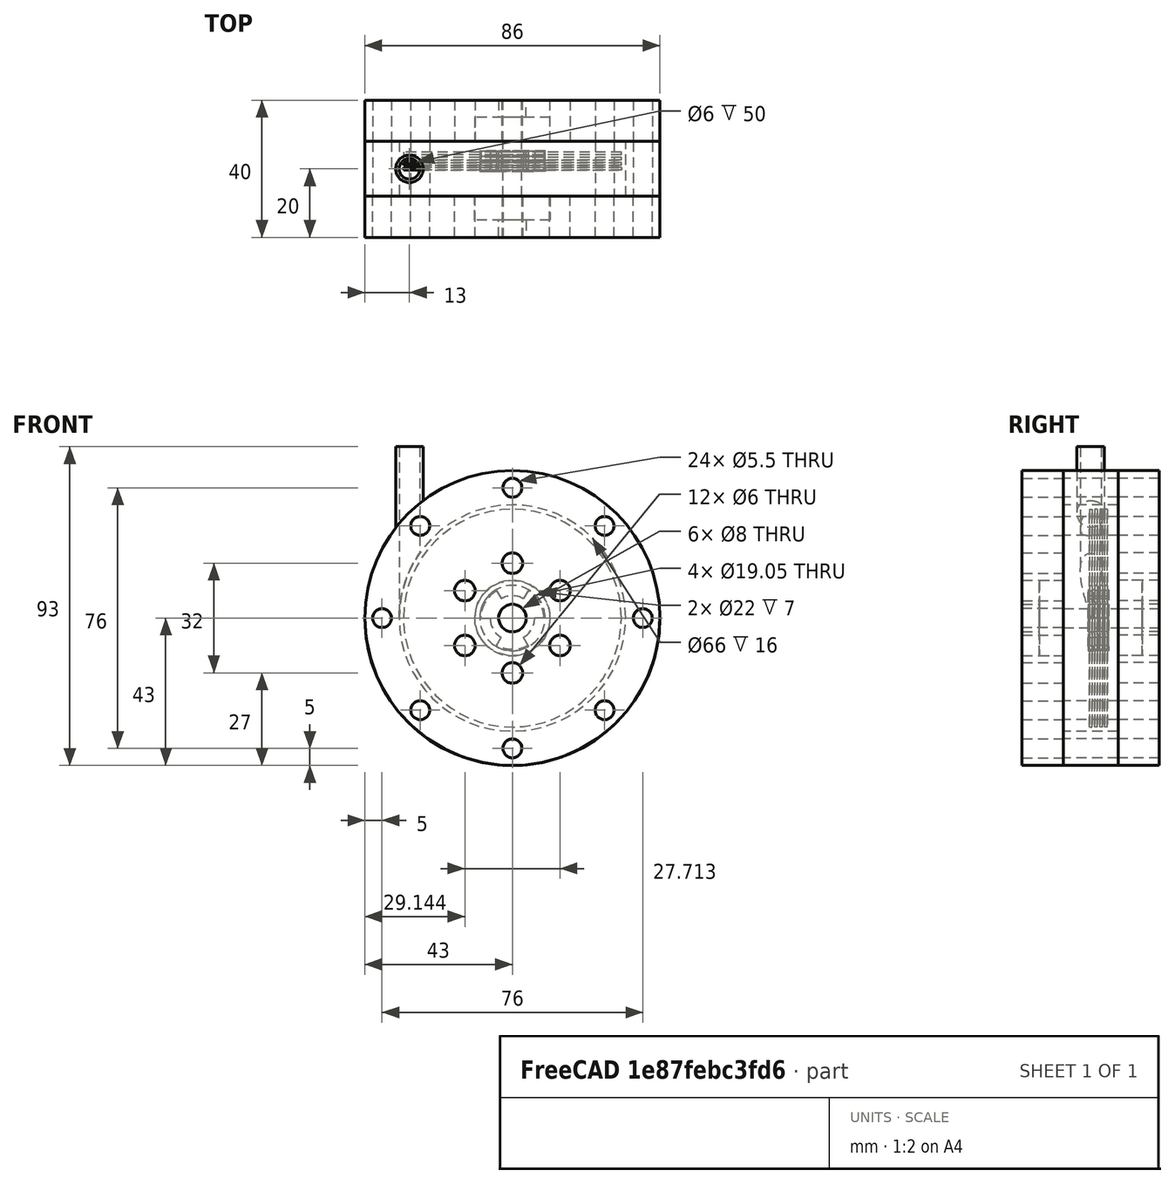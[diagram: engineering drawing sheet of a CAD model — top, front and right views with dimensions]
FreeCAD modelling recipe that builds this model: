
FCSTD DOCUMENT  (FreeCAD 0.17R13541 (Git))
Label: 特斯拉叶轮机 FEM
License: All rights reserved
LicenseURL: http://en.wikipedia.org/wiki/All_rights_reserved
objects: Sketcher::SketchObject×14, PartDesign::ShapeBinder×7, Part::Mirroring×7, Part::Feature×7, PartDesign::Pocket×6, PartDesign::Body×5, PartDesign::Pad×4, PartDesign::PolarPattern×4, PartDesign::Groove×2, Fem::FemMeshShapeNetgenObject×2, PartDesign::Revolution×1, Part::Compound×1, Fem::FemSolverObjectPython×1, Part::MultiFuse×1, Fem::FemAnalysis×1
note: 72 computed .brp shape members not serialized (recipe doc carries the construction recipe); baked Part::Feature solids carry a one-line shape summary decoded from their .brp

FEATURE [Sketcher::SketchObject] Sketch
  MapMode = 5
  Placement = pos=(0,0,0) rot=(1,0,0;1.5708rad)
  Support = -> [XZ_Plane]
  sketch-geometry (14):
    g0: Circle CenterX=0 CenterY=0 CenterZ=0 NormalX=0 NormalY=0 NormalZ=1 AngleXU=0 Radius=4
    g1: Circle CenterX=0 CenterY=0 CenterZ=0 NormalX=0 NormalY=0 NormalZ=1 AngleXU=0 Radius=9.525
    g2: Circle CenterX=0 CenterY=0 CenterZ=0 NormalX=0 NormalY=0 NormalZ=1 AngleXU=0 Radius=43
    g3: Circle CenterX=0 CenterY=0 CenterZ=0 NormalX=0 NormalY=0 NormalZ=1 AngleXU=0 Radius=31.75
    g4: Circle CenterX=0 CenterY=0 CenterZ=0 NormalX=0 NormalY=0 NormalZ=1 AngleXU=0 Radius=33
    g5: LineSegment [constr] StartX=-31.75 StartY=0 StartZ=0 EndX=-33 EndY=0 EndZ=0
    g6: LineSegment [constr] StartX=-33 StartY=0 StartZ=0 EndX=-43 EndY=0 EndZ=0
    g7: LineSegment StartX=-33 StartY=0 StartZ=0 EndX=-30 EndY=0 EndZ=0
    g8: LineSegment StartX=-30 StartY=0 StartZ=0 EndX=-30 EndY=50 EndZ=0
    g9: LineSegment StartX=-30 StartY=50 StartZ=0 EndX=-33 EndY=50 EndZ=0
    g10: LineSegment StartX=-33 StartY=50 StartZ=0 EndX=-33 EndY=0 EndZ=0
    g11: LineSegment StartX=-30 StartY=50 StartZ=0 EndX=-26 EndY=50 EndZ=0
    g12: LineSegment StartX=-26 StartY=50 StartZ=0 EndX=-26 EndY=0 EndZ=0
    g13: LineSegment StartX=-26 StartY=0 StartZ=0 EndX=-30 EndY=0 EndZ=0
  constraints (36):
    c: Coincident(g0,g-1)
    c: Coincident(g1,g-1)
    c: Coincident(g2,g-1)
    c: Coincident(g3,g-1)
    c: Radius(g0) = 4  '轴半径'
    c: Coincident(g4,g-1)
    c: Radius(g1) = 9.525
    c: Radius(g3) = 31.75  '盘片半径'
    c: PointOnObject(g5,g3)
    c: PointOnObject(g5,g4)
    c: Coincident(g6,g5)
    c: PointOnObject(g6,g2)
    c: Horizontal(g6)
    c: PointOnObject(g5,g-1)
    c: Horizontal(g5)
    c: DistanceX(g5,g5) = 1.25  '盘片与腔体内壁间隙'
    c: DistanceX(g6,g5) = 10  '腔体壁厚'
    c: Coincident(g7,g8)
    c: Coincident(g8,g9)
    c: Coincident(g9,g10)
    c: Coincident(g10,g7)
    c: Horizontal(g7)
    c: Horizontal(g9)
    c: Vertical(g8)
    c: Vertical(g10)
    c: Coincident(g7,g5)
    c: Horizontal(g11)
    c: Coincident(g11,g12)
    c: Vertical(g12)
    c: Coincident(g12,g13)
    c: Coincident(g13,g7)
    c: Horizontal(g13)
    c: Coincident(g11,g8)
    c: DistanceX(g8,g11) = 4  '进气管外圆半径'
    c: DistanceX(g9,g8) = 3  '进气管内孔半径'
    c: DistanceY(g5,g9) = 50
FEATURE [PartDesign::Body] Body  label="核心"
  Group = -> [Sketch]
  Origin = -> Origin
FEATURE [PartDesign::ShapeBinder] ShapeBinder
  Support = -> [Sketch]
FEATURE [Sketcher::SketchObject] Sketch001
  ExternalGeometry = -> [ShapeBinder]
  MapMode = 5
  Placement = pos=(0,0,0) rot=(1,0,0;1.5708rad)
  Support = -> [XZ_Plane001]
  sketch-geometry (1):
    g0: Circle CenterX=0 CenterY=0 CenterZ=0 NormalX=0 NormalY=0 NormalZ=1 AngleXU=0 Radius=43
  constraints (2):
    c: Coincident(g0,g-1)
    c: PointOnObject(g-3,g0)
FEATURE [PartDesign::Pad] Pad  label="叶片腔体"
  Length = 16
  Length2 = 100
  Midplane = true
  Placement = pos=(0,0,0) rot=(1,0,0;1.5708rad)
  Profile = -> Sketch001
  Type = 0
FEATURE [Sketcher::SketchObject] Sketch002
  ExternalGeometry = -> [ShapeBinder]
  MapMode = 5
  Placement = pos=(0,0,0) rot=(1,0,0;1.5708rad)
  Support = -> [XZ_Plane001]
  sketch-geometry (4):
    g0: LineSegment StartX=-26 StartY=0 StartZ=0 EndX=-30 EndY=0 EndZ=0
    g1: LineSegment StartX=-30 StartY=0 StartZ=0 EndX=-30 EndY=50 EndZ=0
    g2: LineSegment StartX=-30 StartY=50 StartZ=0 EndX=-26 EndY=50 EndZ=0
    g3: LineSegment StartX=-26 StartY=50 StartZ=0 EndX=-26 EndY=0 EndZ=0
  constraints (10):
    c: Coincident(g0,g1)
    c: Coincident(g1,g2)
    c: Coincident(g2,g3)
    c: Coincident(g3,g0)
    c: Horizontal(g0)
    c: Horizontal(g2)
    c: Vertical(g1)
    c: Vertical(g3)
    c: Coincident(g0,g-4)
    c: Coincident(g1,g-3)
FEATURE [PartDesign::Revolution] Revolution  label="进气管"
  Angle = 360
  Axis = (0,0,1)
  Base = (-30,0,0)
  BaseFeature = -> Pad
  Placement = pos=(0,0,0) rot=(1,0,0;1.5708rad)
  Profile = -> Sketch002
  ReferenceAxis = -> ShapeBinder [Edge14]
FEATURE [Sketcher::SketchObject] Sketch003
  ExternalGeometry = -> [ShapeBinder]
  MapMode = 5
  Placement = pos=(0,0,0) rot=(1,0,0;1.5708rad)
  Support = -> [XZ_Plane001]
  sketch-geometry (1):
    g0: Circle CenterX=0 CenterY=0 CenterZ=0 NormalX=0 NormalY=0 NormalZ=1 AngleXU=0 Radius=33
  constraints (2):
    c: Coincident(g0,g-1)
    c: PointOnObject(g-3,g0)
FEATURE [PartDesign::Pocket] Pocket  label="叶片腔孔"
  BaseFeature = -> Revolution
  Length = 5
  Length2 = 100
  Midplane = true
  Placement = pos=(0,0,0) rot=(1,0,0;1.5708rad)
  Profile = -> Sketch003
  Type = 1
FEATURE [Sketcher::SketchObject] Sketch004
  ExternalGeometry = -> [ShapeBinder]
  MapMode = 5
  Placement = pos=(0,0,0) rot=(1,0,0;1.5708rad)
  Support = -> [XZ_Plane001]
  sketch-geometry (4):
    g0: LineSegment StartX=-30 StartY=50 StartZ=0 EndX=-33 EndY=50 EndZ=0
    g1: LineSegment StartX=-33 StartY=50 StartZ=0 EndX=-33 EndY=0 EndZ=0
    g2: LineSegment StartX=-33 StartY=0 StartZ=0 EndX=-30 EndY=0 EndZ=0
    g3: LineSegment StartX=-30 StartY=0 StartZ=0 EndX=-30 EndY=50 EndZ=0
  constraints (10):
    c: Coincident(g0,g1)
    c: Coincident(g1,g2)
    c: Coincident(g2,g3)
    c: Coincident(g3,g0)
    c: Horizontal(g0)
    c: Horizontal(g2)
    c: Vertical(g1)
    c: Vertical(g3)
    c: Coincident(g0,g-3)
    c: Coincident(g1,g-4)
FEATURE [PartDesign::Groove] Groove  label="进气管孔"
  Angle = 360
  Axis = (0,0,1)
  Base = (-30,0,0)
  BaseFeature = -> Pocket
  Placement = pos=(0,0,0) rot=(1,0,0;1.5708rad)
  Profile = -> Sketch004
  ReferenceAxis = -> ShapeBinder [Edge13]
FEATURE [PartDesign::ShapeBinder] ShapeBinder001
  Support = -> [Sketch]
FEATURE [Sketcher::SketchObject] Sketch005
  ExternalGeometry = -> [ShapeBinder001]
  MapMode = 5
  Placement = pos=(0,0,0) rot=(1,0,0;1.5708rad)
  Support = -> [XZ_Plane002]
  sketch-geometry (2):
    g0: Circle CenterX=0 CenterY=0 CenterZ=0 NormalX=0 NormalY=0 NormalZ=1 AngleXU=0 Radius=9.525
    g1: Circle CenterX=0 CenterY=0 CenterZ=0 NormalX=0 NormalY=0 NormalZ=1 AngleXU=0 Radius=4
  constraints (4):
    c: Coincident(g0,g-1)
    c: Coincident(g1,g-1)
    c: Equal(g1,g-4)
    c: Equal(g-3,g0)
FEATURE [PartDesign::Pad] Pad001  label="分流片基体"
  Length = 1.5
  Length2 = 100
  Midplane = true
  Placement = pos=(0,0,0) rot=(1,0,0;1.5708rad)
  Profile = -> Sketch005
  Type = 0
FEATURE [Sketcher::SketchObject] Sketch006
  ExternalGeometry = -> [ShapeBinder001]
  MapMode = 5
  Placement = pos=(0,0,0) rot=(1,0,0;1.5708rad)
  Support = -> [XZ_Plane002]
  sketch-geometry (8):
    g0: LineSegment [constr] StartX=0 StartY=0 StartZ=0 EndX=4.7625 EndY=8.24889 EndZ=0
    g1: LineSegment [constr] StartX=4.7625 StartY=8.24889 StartZ=0 EndX=-4.7625 EndY=8.24889 EndZ=0
    g2: LineSegment [constr] StartX=-4.7625 StartY=8.24889 StartZ=0 EndX=0 EndY=0 EndZ=0
    g3: Circle [constr] CenterX=0 CenterY=5.49926 CenterZ=0 NormalX=0 NormalY=0 NormalZ=1 AngleXU=0 Radius=5.49926
    g4: ArcOfCircle CenterX=0 CenterY=0 CenterZ=0 NormalX=0 NormalY=0 NormalZ=1 AngleXU=0 Radius=6.5 StartAngle=1.0472 EndAngle=2.0944
    g5: ArcOfCircle CenterX=0 CenterY=0 CenterZ=0 NormalX=0 NormalY=0 NormalZ=1 AngleXU=0 Radius=9.525 StartAngle=1.0472 EndAngle=2.0944
    g6: LineSegment StartX=-4.7625 StartY=8.24889 StartZ=0 EndX=-3.25 EndY=5.62917 EndZ=0
    g7: LineSegment StartX=4.7625 StartY=8.24889 StartZ=0 EndX=3.25 EndY=5.62917 EndZ=0
  constraints (23):
    c: Coincident(g0,g1)
    c: Coincident(g1,g2)
    c: Coincident(g2,g0)
    c: Equal(g0,g1)
    c: Equal(g0,g2)
    c: PointOnObject(g0,g3)
    c: PointOnObject(g1,g3)
    c: PointOnObject(g2,g3)
    c: PointOnObject(g3,g-2)
    c: Coincident(g2,g-1)
    c: PointOnObject(g0,g-3)
    c: Coincident(g4,g-1)
    c: Radius(g4) = 6.5
    c: Coincident(g5,g-1)
    c: Equal(g5,g-3)
    c: PointOnObject(g5,g0)
    c: PointOnObject(g5,g1)
    c: PointOnObject(g4,g0)
    c: PointOnObject(g4,g2)
    c: Coincident(g6,g1)
    c: Coincident(g6,g4)
    c: Coincident(g7,g0)
    c: Coincident(g7,g4)
FEATURE [PartDesign::Pocket] Pocket001  label="分流槽"
  BaseFeature = -> Pad001
  Length = 5
  Length2 = 100
  Midplane = true
  Placement = pos=(0,0,0) rot=(1,0,0;1.5708rad)
  Profile = -> Sketch006
  Type = 1
FEATURE [PartDesign::PolarPattern] PolarPattern  label="分流槽环形阵列"
  Angle = 360
  Axis = -> Sketch006 [N_Axis]
  BaseFeature = -> Pocket001
  Occurrences = 3
  Originals = -> [Pocket001]
  Placement = pos=(0,0,0) rot=(1,0,0;1.5708rad)
FEATURE [Sketcher::SketchObject] Sketch007
  MapMode = 5
  Placement = pos=(0,0,0) rot=(0.57735,0.57735,0.57735;2.0944rad)
  Support = -> [YZ_Plane002]
  sketch-geometry (1):
    g0: Circle CenterX=0 CenterY=9.7 CenterZ=0 NormalX=0 NormalY=0 NormalZ=1 AngleXU=0 Radius=0.5
  constraints (3):
    c: PointOnObject(g0,g-2)
    c: Radius(g0) = 0.5
    c: DistanceY(g-1,g0) = 9.7
FEATURE [PartDesign::Groove] Groove001  label="扶持槽"
  Angle = 360
  Axis = (0,1,0)
  Base = (0,0,0)
  BaseFeature = -> PolarPattern
  Placement = pos=(0,0,0) rot=(1,0,0;1.5708rad)
  Profile = -> Sketch007
  ReferenceAxis = -> Y_Axis002
FEATURE [PartDesign::Body] Body002  label="分流片"
  Group = -> [ShapeBinder001,Sketch005,Pad001,Sketch006,Pocket001,PolarPattern,Sketch007,Groove001]
  Origin = -> Origin002
  Tip = -> Groove001
FEATURE [PartDesign::ShapeBinder] ShapeBinder002  label="引用自核心的线"
  Support = -> [Sketch]
FEATURE [PartDesign::ShapeBinder] ShapeBinder003  label="引用叶片腔的侧面"
  Placement = pos=(0,0,0) rot=(1,0,0;1.5708rad)
  Support = -> [Groove]
FEATURE [Sketcher::SketchObject] Sketch008
  ExternalGeometry = -> [ShapeBinder003,ShapeBinder002]
  MapMode = 5
  Placement = pos=(0,-8,-1e-12) rot=(1,0,0;1.5708rad)
  Support = -> [ShapeBinder003]
  sketch-geometry (2):
    g0: Circle CenterX=0 CenterY=0 CenterZ=0 NormalX=0 NormalY=0 NormalZ=1 AngleXU=0 Radius=4
    g1: Circle CenterX=0 CenterY=0 CenterZ=0 NormalX=0 NormalY=0 NormalZ=1 AngleXU=0 Radius=43
  constraints (4):
    c: Coincident(g0,g-1)
    c: Coincident(g1,g-1)
    c: Equal(g1,g-3)
    c: Equal(g0,g-4)
FEATURE [PartDesign::Pad] Pad002  label="基础"
  Length = 12
  Length2 = 100
  Placement = pos=(0,0,0) rot=(1,0,0;1.5708rad)
  Profile = -> Sketch008
  Type = 0
FEATURE [Sketcher::SketchObject] Sketch009
  MapMode = 5
  Placement = pos=(0,-8,-1e-12) rot=(-1,0,0;1.5708rad)
  Support = -> [Pad002]
  sketch-geometry (1):
    g0: Circle CenterX=0 CenterY=0 CenterZ=0 NormalX=0 NormalY=0 NormalZ=1 AngleXU=0 Radius=11
  constraints (2):
    c: Coincident(g0,g-1)
    c: Radius(g0) = 11
FEATURE [PartDesign::Pocket] Pocket002  label="轴承孔"
  BaseFeature = -> Pad002
  Length = 7
  Length2 = 100
  Placement = pos=(0,0,0) rot=(1,0,0;1.5708rad)
  Profile = -> Sketch009
  Type = 0
FEATURE [Sketcher::SketchObject] Sketch010
  MapMode = 5
  Placement = pos=(0,-8,-1e-12) rot=(-1,0,0;1.5708rad)
  Support = -> [Pocket002]
  sketch-geometry (1):
    g0: Circle CenterX=0 CenterY=16 CenterZ=0 NormalX=0 NormalY=0 NormalZ=1 AngleXU=0 Radius=3
  constraints (3):
    c: PointOnObject(g0,g-2)
    c: Radius(g0) = 3
    c: DistanceY(g-1,g0) = 16
FEATURE [PartDesign::Pocket] Pocket003  label="出气孔"
  BaseFeature = -> Pocket002
  Length = 5
  Length2 = 100
  Placement = pos=(0,0,0) rot=(1,0,0;1.5708rad)
  Profile = -> Sketch010
  Type = 1
FEATURE [PartDesign::PolarPattern] PolarPattern001  label="出气孔环形阵列"
  Angle = 360
  Axis = -> Sketch010 [N_Axis]
  BaseFeature = -> Pocket003
  Occurrences = 6
  Originals = -> [Pocket003]
  Placement = pos=(0,0,0) rot=(1,0,0;1.5708rad)
FEATURE [Sketcher::SketchObject] Sketch011
  ExternalGeometry = -> [ShapeBinder002]
  MapMode = 5
  Placement = pos=(0,-8,-1e-12) rot=(-1,0,0;1.5708rad)
  Support = -> [PolarPattern001]
  sketch-geometry (2):
    g0: Circle CenterX=0 CenterY=38 CenterZ=0 NormalX=0 NormalY=0 NormalZ=1 AngleXU=0 Radius=2.75
    g1: LineSegment [constr] StartX=0 StartY=38 StartZ=0 EndX=0 EndY=33 EndZ=0
  constraints (6):
    c: PointOnObject(g0,g-2)
    c: Radius(g0) = 2.75
    c: Coincident(g1,g0)
    c: PointOnObject(g1,g-3)
    c: Vertical(g1)
    c: DistanceY(g1,g0) = 5
FEATURE [PartDesign::Pocket] Pocket004  label="安装孔"
  BaseFeature = -> PolarPattern001
  Length = 5
  Length2 = 100
  Placement = pos=(0,0,0) rot=(1,0,0;1.5708rad)
  Profile = -> Sketch011
  Type = 1
FEATURE [PartDesign::PolarPattern] PolarPattern002  label="安装孔环形阵列"
  Angle = 360
  Axis = -> Sketch011 [N_Axis]
  BaseFeature = -> Pocket004
  Occurrences = 8
  Originals = -> [Pocket004]
  Placement = pos=(0,0,0) rot=(1,0,0;1.5708rad)
FEATURE [PartDesign::Body] Body003  label="盖板甲"
  Group = -> [ShapeBinder002,ShapeBinder003,Sketch008,Pad002,Sketch009,Pocket002,Sketch010,Pocket003,PolarPattern001,Sketch011,Pocket004,PolarPattern002]
  Origin = -> Origin003
  Tip = -> PolarPattern002
FEATURE [Part::Mirroring] Part__Mirroring  label="盖板乙"
  Base = (0,0,-1.66893e-06)
  Normal = (0,1,-1.19209e-07)
  Source = -> PolarPattern002
FEATURE [PartDesign::ShapeBinder] ShapeBinder004
  Support = -> [Sketch]
FEATURE [PartDesign::ShapeBinder] ShapeBinder005
  Placement = pos=(0,0,0) rot=(1,0,0;1.5708rad)
  Support = -> [Groove001]
FEATURE [Sketcher::SketchObject] Sketch012
  ExternalGeometry = -> [ShapeBinder005,ShapeBinder004]
  MapMode = 5
  Placement = pos=(0,0,0) rot=(1,0,0;1.5708rad)
  Support = -> [XZ_Plane004]
  sketch-geometry (2):
    g0: Circle CenterX=0 CenterY=0 CenterZ=0 NormalX=0 NormalY=0 NormalZ=1 AngleXU=0 Radius=9.525
    g1: Circle CenterX=0 CenterY=0 CenterZ=0 NormalX=0 NormalY=0 NormalZ=1 AngleXU=0 Radius=31.75
  constraints (4):
    c: Coincident(g0,g-1)
    c: Coincident(g1,g-1)
    c: Equal(g1,g-4)
    c: Equal(g0,g-3)
FEATURE [PartDesign::Pad] Pad003
  Length = 0.75
  Length2 = 100
  Midplane = true
  Placement = pos=(0,0,0) rot=(1,0,0;1.5708rad)
  Profile = -> Sketch012
  Type = 0
FEATURE [PartDesign::Body] Body004  label="盘片"
  Group = -> [ShapeBinder004,ShapeBinder005,Sketch012,Pad003]
  Origin = -> Origin004
  Tip = -> Pad003
FEATURE [Part::Feature] Body002001  label="分流片001"
  Placement = pos=(0,-1.5,0) rot=(0,0,1;0rad)
  shape: bbox 19.05 x 1.5 x 17.77 mm, 21 faces (baked)
FEATURE [Part::Feature] Body002002  label="分流片002"
  Placement = pos=(0,-3,0) rot=(0,0,1;0rad)
  shape: bbox 19.05 x 1.5 x 17.77 mm, 21 faces (baked)
FEATURE [Part::Feature] Body002003  label="分流片003"
  Placement = pos=(0,-4.5,0) rot=(0,0,1;0rad)
  shape: bbox 19.05 x 1.5 x 17.77 mm, 21 faces (baked)
FEATURE [Part::Feature] Body004001  label="盘片001"
  Placement = pos=(0,-1.5,0) rot=(0,0,1;0rad)
  shape: bbox 63.5 x 0.75 x 63.5 mm, 4 faces (baked)
FEATURE [Part::Feature] Body004002  label="盘片002"
  Placement = pos=(0,-3,0) rot=(0,0,1;0rad)
  shape: bbox 63.5 x 0.75 x 63.5 mm, 4 faces (baked)
FEATURE [Part::Feature] Body004003  label="盘片003"
  Placement = pos=(0,-4.5,0) rot=(0,0,1;0rad)
  shape: bbox 63.5 x 0.75 x 63.5 mm, 4 faces (baked)
FEATURE [Part::Mirroring] Part__Mirroring001  label="分流片001 (Mirror #2)"
  Base = (0,0,0)
  Normal = (0,1,0)
  Source = -> Body002001
FEATURE [Part::Mirroring] Part__Mirroring002  label="分流片002 (Mirror #3)"
  Base = (0,0,0)
  Normal = (0,1,0)
  Source = -> Body002002
FEATURE [Part::Mirroring] Part__Mirroring003  label="分流片003 (Mirror #4)"
  Base = (0,0,0)
  Normal = (0,1,0)
  Source = -> Body002003
FEATURE [Part::Mirroring] Part__Mirroring004  label="盘片001 (Mirror #5)"
  Base = (0,0,0)
  Normal = (0,1,0)
  Source = -> Body004001
FEATURE [Part::Mirroring] Part__Mirroring005  label="盘片002 (Mirror #6)"
  Base = (0,0,0)
  Normal = (0,1,0)
  Source = -> Body004002
FEATURE [Part::Mirroring] Part__Mirroring006  label="盘片003 (Mirror #7)"
  Base = (0,0,0)
  Normal = (0,1,0)
  Source = -> Body004003
FEATURE [Part::Compound] Compound  label="分流片和盘片的副本"
  Links = -> [Part__Mirroring001,Part__Mirroring006,Part__Mirroring005,Part__Mirroring004,Part__Mirroring002,Part__Mirroring003]
FEATURE [PartDesign::ShapeBinder] ShapeBinder006  label="引用自盖板甲的内侧面"
  Placement = pos=(0,0,0) rot=(1,0,0;1.5708rad)
  Support = -> [PolarPattern002]
FEATURE [Sketcher::SketchObject] Sketch013
  ExternalGeometry = -> [ShapeBinder006]
  MapMode = 5
  Placement = pos=(0,-8,-1e-12) rot=(1,0,0;1.5708rad)
  Support = -> [Groove]
  sketch-geometry (1):
    g0: Circle CenterX=0 CenterY=-38 CenterZ=0 NormalX=0 NormalY=0 NormalZ=1 AngleXU=0 Radius=2.75
  constraints (2):
    c: Coincident(g0,g-3)
    c: Equal(g0,g-3)
FEATURE [PartDesign::Pocket] Pocket005
  BaseFeature = -> Groove
  Length = 5
  Length2 = 100
  Placement = pos=(0,0,0) rot=(1,0,0;1.5708rad)
  Profile = -> Sketch013
  Type = 1
FEATURE [PartDesign::PolarPattern] PolarPattern003
  Angle = 360
  Axis = -> Sketch013 [N_Axis]
  BaseFeature = -> Pocket005
  Occurrences = 8
  Originals = -> [Pocket005]
  Placement = pos=(0,0,0) rot=(1,0,0;1.5708rad)
FEATURE [PartDesign::Body] Body001  label="叶片腔"
  Group = -> [ShapeBinder,Sketch001,Pad,Sketch002,Revolution,Sketch003,Pocket,Sketch004,Groove,ShapeBinder006,Sketch013,Pocket005,PolarPattern003]
  Origin = -> Origin001
  Tip = -> PolarPattern003
FEATURE [Part::Feature] Body001001  label="叶片腔001"
  shape: bbox 86 x 16 x 93 mm, 15 faces (baked)
FEATURE [Fem::FemSolverObjectPython] CalculiXccxTools  # FEM object (typed FeaturePython)
  AnalysisType = 0
  BeamShellResultOutput3D = false
  EigenmodeHighLimit = 1000000
  EigenmodeLowLimit = 0
  EigenmodesCount = 10
  GeometricalNonlinearity = 0
  IterationsControlParameterCutb = 0.25,0.5,0.75,0.85,,,1.5,
  IterationsControlParameterIter = 4,8,9,200,10,400,,200,,
  IterationsControlParameterTimeUse = false
  IterationsThermoMechMaximum = 2000
  IterationsUserDefinedIncrementations = false
  IterationsUserDefinedTimeStepLength = false
  MaterialNonlinearity = 0
  MatrixSolverType = 0
  SplitInputWriter = false
  ThermoMechSteadyState = true
  TimeEnd = 1
  TimeInitialStep = 0.01
FEATURE [Fem::FemMeshShapeNetgenObject] FEMMeshNetgen  label="Housing"
  Fineness = 2
  GrowthRate = 0.3
  MaxSize = 1000
  NbSegsPerEdge = 1
  NbSegsPerRadius = 2
  Optimize = true
  SecondOrder = true
  Shape = -> Body001001
FEATURE [Part::MultiFuse] Fusion
  Shapes = -> [Body002,Body004,Compound]
FEATURE [Fem::FemMeshShapeNetgenObject] FEMMeshNetgen001  label="Plants"
  Fineness = 2
  GrowthRate = 0.3
  MaxSize = 1000
  NbSegsPerEdge = 1
  NbSegsPerRadius = 2
  Optimize = true
  SecondOrder = true
  Shape = -> Fusion
FEATURE [Fem::FemAnalysis] Analysis
  Group = -> [CalculiXccxTools,FEMMeshNetgen,FEMMeshNetgen001]
